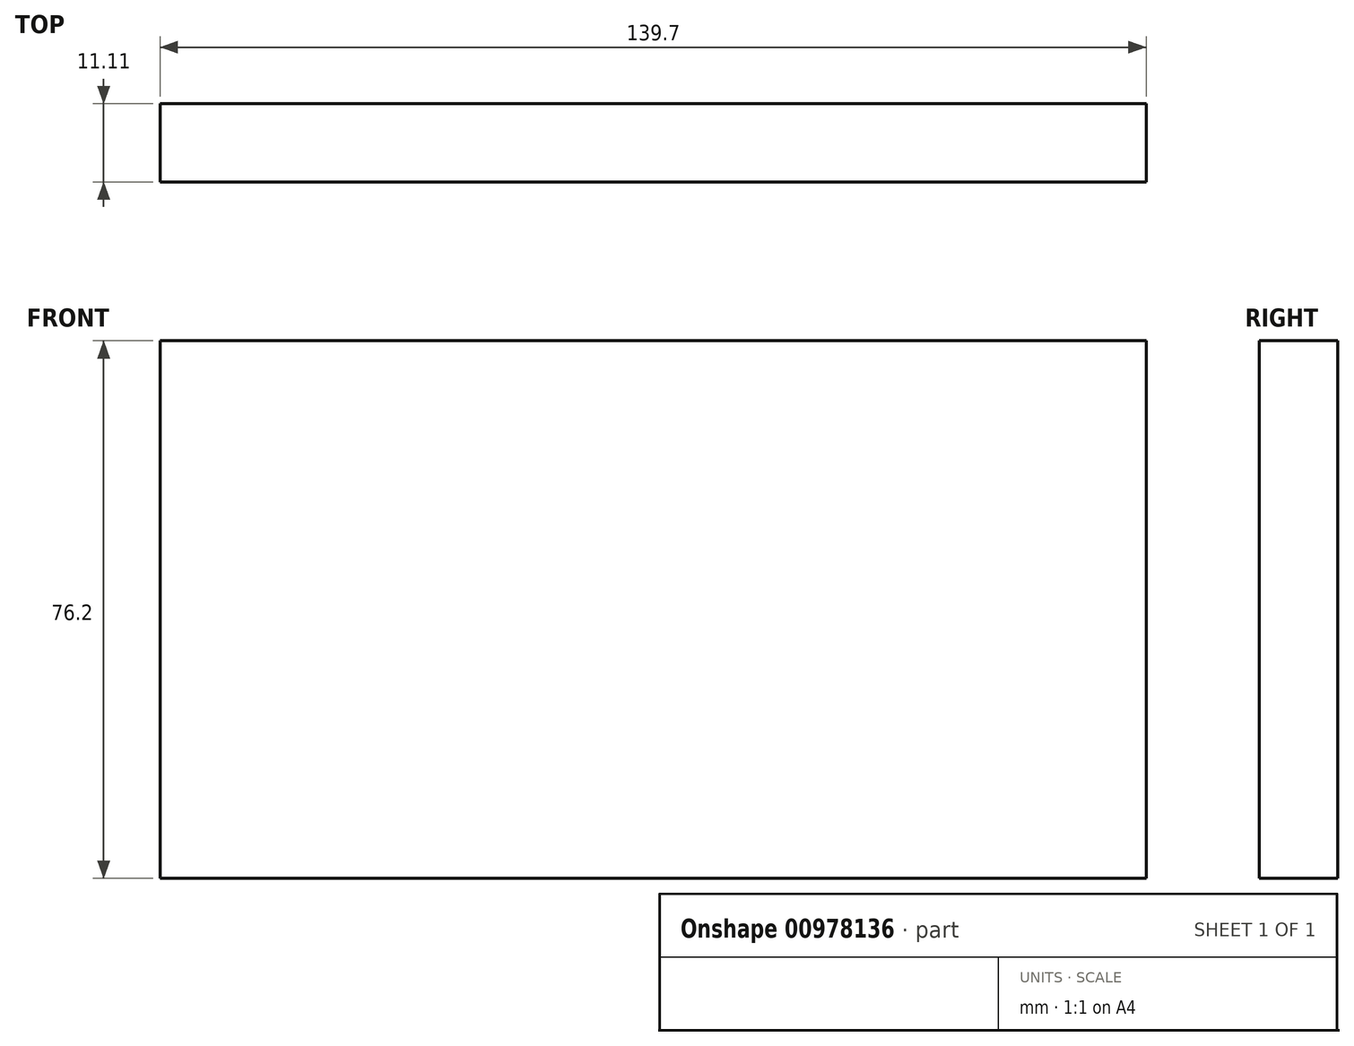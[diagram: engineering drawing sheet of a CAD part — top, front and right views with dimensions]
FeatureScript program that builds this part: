
annotation { "Feature Type Name" : "Feature", "Feature Type Description" : "" }
export const myFeature = defineFeature(function(context is Context, id is Id, definition is map)
    precondition{}
    {
        {
            var Q0;
            Q0=qCreatedBy(makeId("Front.planeOp"),FACE);
            var sketch = newSketch(context, id + "F0", { "sketchPlane" : qUnion([Q0])});
            skLineSegment(sketch, "E0.bottom", {"start": v(69.85, 38.1) * mm, "end": v(-69.85, 38.1) * mm});
            skLineSegment(sketch, "E0.top", {"start": v(69.85, -38.1) * mm, "end": v(-69.85, -38.1) * mm});
            skLineSegment(sketch, "E0.left", {"start": v(69.85, 38.1) * mm, "end": v(69.85, -38.1) * mm});
            skLineSegment(sketch, "E0.right", {"start": v(-69.85, 38.1) * mm, "end": v(-69.85, -38.1) * mm});
            skPoint(sketch, "E0.middle", {"position": v(0, 0) * mm});
            skSolve(sketch);
        }
        {
            var Q0;
            Q0=makeQuery(id+"F0.imprint","IMPRINT",FACE,{"disambiguationData":[TD([[makeQuery(id+"F0.imprint","IMPRINT",EDGE,{"derivedFrom":sQuery(id+"F0.wireOp",EDGE,"E0.bottom")}),1.0]])]});
            extrude(context, id + "F1", {"entities" : qUnion([Q0]), "depth" : 11.1 * mm, "offsetDistance" : 25.4 * mm});
        }
    });
